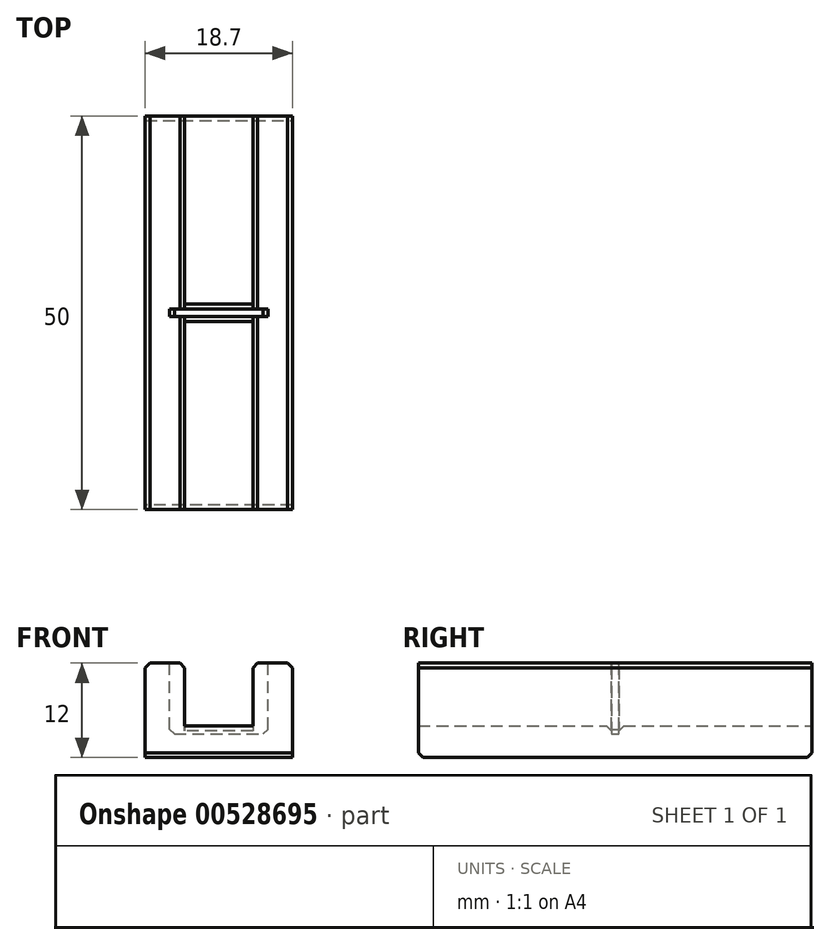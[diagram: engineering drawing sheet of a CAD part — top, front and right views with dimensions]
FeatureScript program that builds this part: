
annotation { "Feature Type Name" : "Feature", "Feature Type Description" : "" }
export const myFeature = defineFeature(function(context is Context, id is Id, definition is map)
    precondition{}
    {
        {
            var Q0;
            Q0=qCreatedBy(makeId("Front.planeOp"),FACE);
            var sketch = newSketch(context, id + "F0", { "sketchPlane" : qUnion([Q0])});
            skLineSegment(sketch, "E0.bottom", {"start": v(9.35, -6) * mm, "end": v(-9.35, -6) * mm});
            skLineSegment(sketch, "E0.top", {"start": v(9.35, 6) * mm, "end": v(-9.35, 6) * mm});
            skLineSegment(sketch, "E0.left", {"start": v(9.35, -6) * mm, "end": v(9.35, 6) * mm});
            skLineSegment(sketch, "E0.right", {"start": v(-9.35, -6) * mm, "end": v(-9.35, 6) * mm});
            skPoint(sketch, "E0.middle", {"position": v(0, 0) * mm});
            skLineSegment(sketch, "E1.bottom", {"start": v(4.35, 6) * mm, "end": v(-4.35, 6) * mm});
            skLineSegment(sketch, "E1.top", {"start": v(4.35, -2) * mm, "end": v(-4.35, -2) * mm});
            skLineSegment(sketch, "E1.left", {"start": v(4.35, 6) * mm, "end": v(4.35, -2) * mm});
            skLineSegment(sketch, "E1.right", {"start": v(-4.35, 6) * mm, "end": v(-4.35, -2) * mm});
            skPoint(sketch, "E1.middle", {"position": v(0, 2) * mm});
            skSolve(sketch);
        }
        {
            var Q0;
            Q0=makeQuery(id+"F0.imprint","IMPRINT",FACE,{"disambiguationData":[TD([[makeQuery(id+"F0.imprint","IMPRINT",EDGE,{"derivedFrom":sQuery(id+"F0.wireOp",EDGE,"E0.bottom")}),-1.0]])]});
            extrude(context, id + "F1", {"entities" : qUnion([Q0]), "endBound" : BoundingType.SYMMETRIC, "depth" : 50 * mm, "offsetDistance" : 25 * mm});
        }
        {
            var Q0;
            {var subQ0=sQuery(id+"F0.wireOp",EDGE,"E0.top");Q0=makeQuery(id+"F1.opExtrude","SWEPT_FACE",FACE,{"disambiguationData":[OSD([subQ0]),TDD([makeQuery(id+"F0.imprint","IMPRINT",EDGE,{"disambiguationData":[TD([[makeQuery(id+"F0.imprint","INTERSECT",VERTEX,{"derivedFrom":[subQ0,sQuery(id+"F0.wireOp",EDGE,"E0.left")]}),-1.0]])],"derivedFrom":subQ0})])]});}
            var sketch = newSketch(context, id + "F2", { "sketchPlane" : qUnion([Q0])});
            skLineSegment(sketch, "E2.bottom", {"start": v(-6.25, -0.5) * mm, "end": v(6.25, -0.5) * mm});
            skLineSegment(sketch, "E2.top", {"start": v(-6.25, 0.5) * mm, "end": v(6.25, 0.5) * mm});
            skLineSegment(sketch, "E2.left", {"start": v(-6.25, -0.5) * mm, "end": v(-6.25, 0.5) * mm});
            skLineSegment(sketch, "E2.right", {"start": v(6.25, -0.5) * mm, "end": v(6.25, 0.5) * mm});
            skPoint(sketch, "E2.middle", {"position": v(0, 0) * mm});
            skSolve(sketch);
        }
        {
            var Q0;
            {var subQ0=sQuery(id+"F2.wireOp",EDGE,"E2.right");Q0=makeQuery(id+"F2.imprint","IMPRINT",FACE,{"disambiguationData":[TD([[makeQuery(id+"F2.imprint","IMPRINT",EDGE,{"derivedFrom":subQ0}),1.0]])]});}
            var Q1;
            {var subQ0=sQuery(id+"F2.wireOp",EDGE,"E2.left");Q1=makeQuery(id+"F2.imprint","IMPRINT",FACE,{"disambiguationData":[TD([[makeQuery(id+"F2.imprint","IMPRINT",EDGE,{"derivedFrom":subQ0}),-1.0]])]});}
            var Q2;
            Q2=makeQuery(id+"F1.opExtrude","SWEPT_FACE",FACE,{"disambiguationData":[OSD([sQuery(id+"F0.wireOp",EDGE,"E1.top")])]});
            extrude(context, id + "F3", {"entities" : qUnion([Q0, Q1]), "operationType" : NewBodyOperationType.REMOVE, "oppositeDirection" : true, "depth" : 9 * mm, "endBoundEntityFace" : qUnion([Q2]), "offsetDistance" : 25 * mm});
        }
        {
            var Q0;
            {var subQ0=sQuery(id+"F0.wireOp",EDGE,"E0.top");var subQ1=sQuery(id+"F2.wireOp",EDGE,"E2.top");Q0=makeQuery(id+"F3.boolean.opBoolean","COPY",EDGE,{"disambiguationData":[topologyDisambiguationEdgeConnected([makeQuery(id+"F1.opExtrude","SWEPT_FACE",FACE,{"disambiguationData":[OSD([subQ0]),TDD([makeQuery(id+"F0.imprint","IMPRINT",EDGE,{"disambiguationData":[TD([[makeQuery(id+"F0.imprint","INTERSECT",VERTEX,{"derivedFrom":[subQ0,sQuery(id+"F0.wireOp",EDGE,"E0.left")]}),-1.0]])],"derivedFrom":subQ0})])]})])],"derivedFrom":makeQuery(id+"F3.opExtrude","CAP_EDGE",EDGE,{"disambiguationData":[OSD([subQ1])],"isStart":true})});}
            var Q1;
            Q1=makeQuery(id+"F3.boolean.opBoolean","COPY",EDGE,{"derivedFrom":makeQuery(id+"F3.opExtrude","CAP_EDGE",EDGE,{"disambiguationData":[OSD([sQuery(id+"F2.wireOp",EDGE,"E2.right")])],"isStart":true})});
            var Q2;
            {var subQ0=sQuery(id+"F0.wireOp",EDGE,"E0.top");var subQ1=sQuery(id+"F2.wireOp",EDGE,"E2.bottom");Q2=makeQuery(id+"F3.boolean.opBoolean","COPY",EDGE,{"disambiguationData":[topologyDisambiguationEdgeConnected([makeQuery(id+"F1.opExtrude","SWEPT_FACE",FACE,{"disambiguationData":[OSD([subQ0]),TDD([makeQuery(id+"F0.imprint","IMPRINT",EDGE,{"disambiguationData":[TD([[makeQuery(id+"F0.imprint","INTERSECT",VERTEX,{"derivedFrom":[subQ0,sQuery(id+"F0.wireOp",EDGE,"E0.left")]}),-1.0]])],"derivedFrom":subQ0})])]})])],"derivedFrom":makeQuery(id+"F3.opExtrude","CAP_EDGE",EDGE,{"disambiguationData":[OSD([subQ1])],"isStart":true})});}
            var Q3;
            {var subQ0=sQuery(id+"F0.wireOp",EDGE,"E0.top");var subQ1=sQuery(id+"F2.wireOp",EDGE,"E2.top");Q3=makeQuery(id+"F3.boolean.opBoolean","COPY",EDGE,{"disambiguationData":[topologyDisambiguationEdgeConnected([makeQuery(id+"F1.opExtrude","SWEPT_FACE",FACE,{"disambiguationData":[OSD([subQ0]),TDD([makeQuery(id+"F0.imprint","IMPRINT",EDGE,{"disambiguationData":[TD([[makeQuery(id+"F0.imprint","INTERSECT",VERTEX,{"derivedFrom":[subQ0,sQuery(id+"F0.wireOp",EDGE,"E0.right")]}),1.0]])],"derivedFrom":subQ0})])]})])],"derivedFrom":makeQuery(id+"F3.opExtrude","CAP_EDGE",EDGE,{"disambiguationData":[OSD([subQ1])],"isStart":true})});}
            var Q4;
            Q4=makeQuery(id+"F3.boolean.opBoolean","COPY",EDGE,{"derivedFrom":makeQuery(id+"F3.opExtrude","CAP_EDGE",EDGE,{"disambiguationData":[OSD([sQuery(id+"F2.wireOp",EDGE,"E2.left")])],"isStart":true})});
            var Q5;
            {var subQ0=sQuery(id+"F0.wireOp",EDGE,"E0.top");var subQ1=sQuery(id+"F2.wireOp",EDGE,"E2.bottom");Q5=makeQuery(id+"F3.boolean.opBoolean","COPY",EDGE,{"disambiguationData":[topologyDisambiguationEdgeConnected([makeQuery(id+"F1.opExtrude","SWEPT_FACE",FACE,{"disambiguationData":[OSD([subQ0]),TDD([makeQuery(id+"F0.imprint","IMPRINT",EDGE,{"disambiguationData":[TD([[makeQuery(id+"F0.imprint","INTERSECT",VERTEX,{"derivedFrom":[subQ0,sQuery(id+"F0.wireOp",EDGE,"E0.right")]}),1.0]])],"derivedFrom":subQ0})])]})])],"derivedFrom":makeQuery(id+"F3.opExtrude","CAP_EDGE",EDGE,{"disambiguationData":[OSD([subQ1])],"isStart":true})});}
            var Q6;
            {var subQ0=sQuery(id+"F0.wireOp",EDGE,"E1.left");var subQ2=sQuery(id+"F0.wireOp",EDGE,"E0.top");var subQ3=sQuery(id+"F0.wireOp",EDGE,"E1.bottom");Q6=makeQuery(id+"F3.boolean.opBoolean","SPLIT",EDGE,{"disambiguationData":[TD([makeQuery(id+"F3.opExtrude","SWEPT_FACE",FACE,{"disambiguationData":[OSD([sQuery(id+"F2.wireOp",EDGE,"E2.top")])]})])],"derivedFrom":makeQuery(id+"F1.opExtrude","SWEPT_EDGE",EDGE,{"disambiguationData":[OSD([subQ2,subQ3,subQ0])]})});}
            var Q7;
            {var subQ0=sQuery(id+"F0.wireOp",EDGE,"E1.left");var subQ2=sQuery(id+"F0.wireOp",EDGE,"E0.top");var subQ3=sQuery(id+"F0.wireOp",EDGE,"E1.bottom");Q7=makeQuery(id+"F3.boolean.opBoolean","SPLIT",EDGE,{"disambiguationData":[TD([makeQuery(id+"F3.opExtrude","SWEPT_FACE",FACE,{"disambiguationData":[OSD([sQuery(id+"F2.wireOp",EDGE,"E2.bottom")])]})])],"derivedFrom":makeQuery(id+"F1.opExtrude","SWEPT_EDGE",EDGE,{"disambiguationData":[OSD([subQ2,subQ3,subQ0])]})});}
            var Q8;
            Q8=makeQuery(id+"F1.opExtrude","SWEPT_EDGE",EDGE,{"disambiguationData":[OSD([sQuery(id+"F0.wireOp",EDGE,"E0.top"),sQuery(id+"F0.wireOp",EDGE,"E0.left")])]});
            var Q9;
            {var subQ0=sQuery(id+"F0.wireOp",EDGE,"E1.right");var subQ2=sQuery(id+"F0.wireOp",EDGE,"E0.top");var subQ3=sQuery(id+"F0.wireOp",EDGE,"E1.bottom");Q9=makeQuery(id+"F3.boolean.opBoolean","SPLIT",EDGE,{"disambiguationData":[TD([makeQuery(id+"F3.opExtrude","SWEPT_FACE",FACE,{"disambiguationData":[OSD([sQuery(id+"F2.wireOp",EDGE,"E2.bottom")])]})])],"derivedFrom":makeQuery(id+"F1.opExtrude","SWEPT_EDGE",EDGE,{"disambiguationData":[OSD([subQ2,subQ3,subQ0])]})});}
            var Q10;
            {var subQ0=sQuery(id+"F0.wireOp",EDGE,"E1.right");var subQ2=sQuery(id+"F0.wireOp",EDGE,"E0.top");var subQ3=sQuery(id+"F0.wireOp",EDGE,"E1.bottom");Q10=makeQuery(id+"F3.boolean.opBoolean","SPLIT",EDGE,{"disambiguationData":[TD([makeQuery(id+"F3.opExtrude","SWEPT_FACE",FACE,{"disambiguationData":[OSD([sQuery(id+"F2.wireOp",EDGE,"E2.top")])]})])],"derivedFrom":makeQuery(id+"F1.opExtrude","SWEPT_EDGE",EDGE,{"disambiguationData":[OSD([subQ2,subQ3,subQ0])]})});}
            var Q11;
            Q11=makeQuery(id+"F1.opExtrude","SWEPT_EDGE",EDGE,{"disambiguationData":[OSD([sQuery(id+"F0.wireOp",EDGE,"E0.top"),sQuery(id+"F0.wireOp",EDGE,"E0.right")])]});
            var Q12;
            Q12=makeQuery(id+"F1.opExtrude","CAP_EDGE",EDGE,{"disambiguationData":[OSD([sQuery(id+"F0.wireOp",EDGE,"E0.bottom")])],"isStart":true});
            var Q13;
            Q13=makeQuery(id+"F1.opExtrude","CAP_EDGE",EDGE,{"disambiguationData":[OSD([sQuery(id+"F0.wireOp",EDGE,"E0.bottom")])],"isStart":false});
            var Q14;
            Q14=makeQuery(id+"F3.boolean.opBoolean","COPY",EDGE,{"derivedFrom":makeQuery(id+"F3.opExtrude","CAP_EDGE",EDGE,{"disambiguationData":[OSD([sQuery(id+"F2.wireOp",EDGE,"E2.left")])],"isStart":false})});
            var Q15;
            Q15=makeQuery(id+"F3.boolean.opBoolean","COPY",EDGE,{"derivedFrom":makeQuery(id+"F3.opExtrude","CAP_EDGE",EDGE,{"disambiguationData":[OSD([sQuery(id+"F2.wireOp",EDGE,"E2.right")])],"isStart":false})});
            var Q16;
            Q16=makeQuery(id+"F3.boolean.opBoolean","INTERSECT",EDGE,{"derivedFrom":[makeQuery(id+"F1.opExtrude","SWEPT_FACE",FACE,{"disambiguationData":[OSD([sQuery(id+"F0.wireOp",EDGE,"E1.top")])]}),makeQuery(id+"F3.opExtrude","SWEPT_FACE",FACE,{"disambiguationData":[OSD([sQuery(id+"F2.wireOp",EDGE,"E2.top")])]})]});
            var Q17;
            Q17=makeQuery(id+"F3.boolean.opBoolean","INTERSECT",EDGE,{"derivedFrom":[makeQuery(id+"F1.opExtrude","SWEPT_FACE",FACE,{"disambiguationData":[OSD([sQuery(id+"F0.wireOp",EDGE,"E1.top")])]}),makeQuery(id+"F3.opExtrude","SWEPT_FACE",FACE,{"disambiguationData":[OSD([sQuery(id+"F2.wireOp",EDGE,"E2.bottom")])]})]});
            chamfer(context, id + "F4", {"entities" : qUnion([Q0, Q1, Q2, Q3, Q4, Q5, Q6, Q7, Q8, Q9, Q10, Q11, Q12, Q13, Q14, Q15, Q16, Q17]), "width" : .6 * mm, "tangentPropagation" : true});
        }
    });
